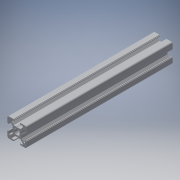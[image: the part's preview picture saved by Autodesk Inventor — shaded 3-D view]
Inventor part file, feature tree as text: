
AUTODESK INVENTOR PART (.ipt)
format: ipt  version: 2019 (Build 230136000, 136)  size: 317,952 bytes
history: native  units: in
note: dims shown in document units (in); Inventor stores cm internally (conversion verified against a paired STEP export)
features: other x3, extrude x1, sketch x1
ambient origin geometry x8: Origin, YZ Plane, XZ Plane, XY Plane, X Axis, Y Axis, Z Axis, Center Point
bodies: Solid1 (feature_tree)
feature tree (5):
  other  "Blocks"
  extrude  "Extrusion1"  Depth=1.0in
  sketch  "Sketch1"  dims[d1=0.0in d13=1.0in d14=1.0in]
  other  "20x20"
  other  "20x20:1"
